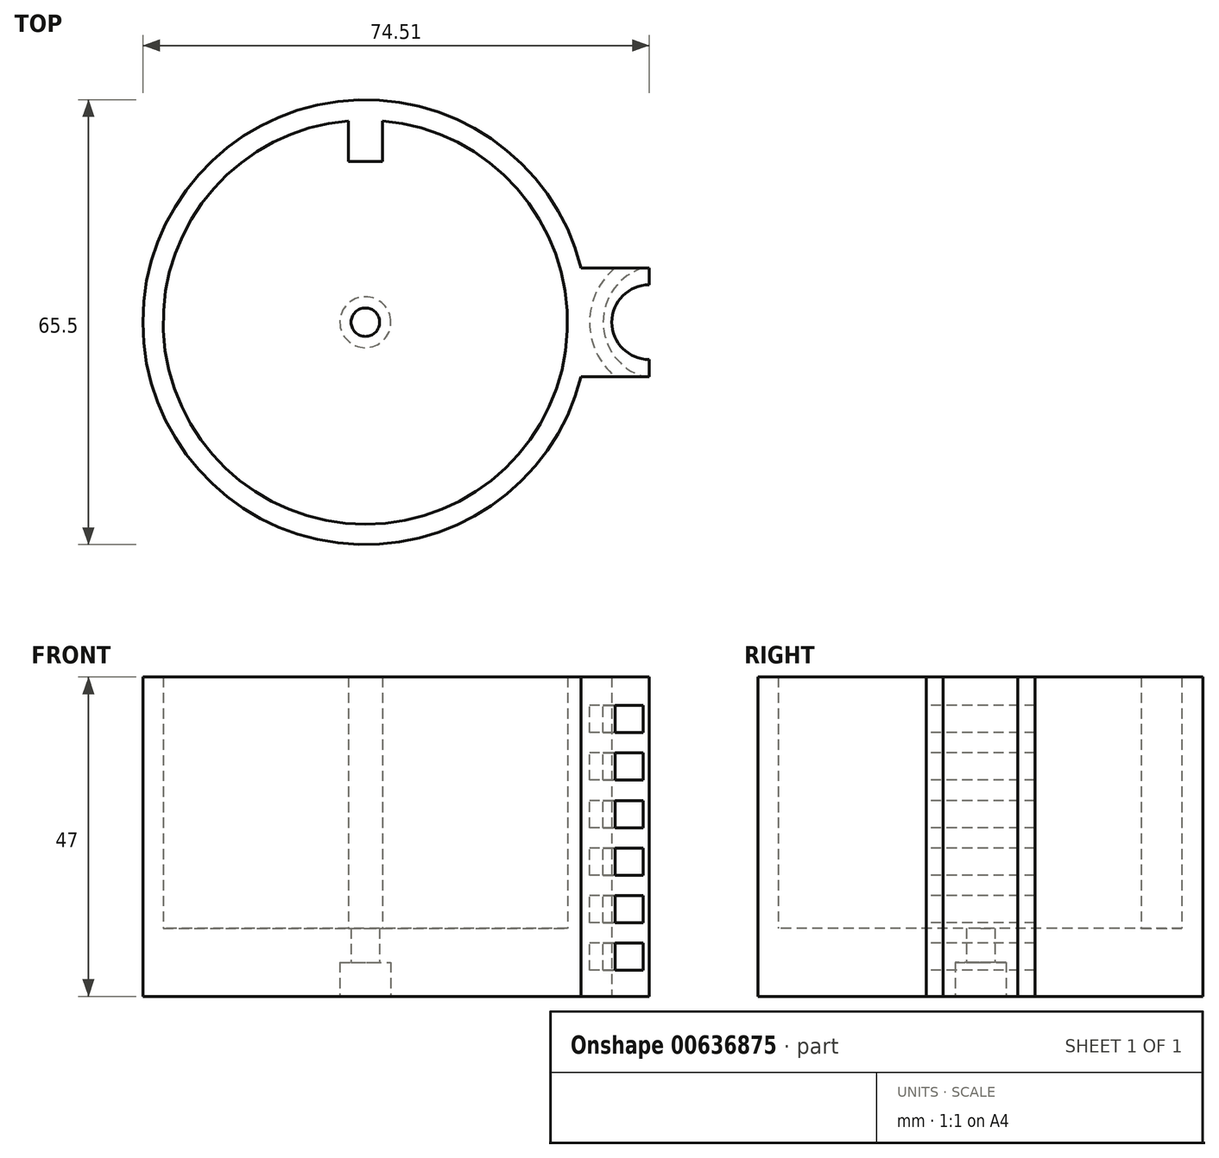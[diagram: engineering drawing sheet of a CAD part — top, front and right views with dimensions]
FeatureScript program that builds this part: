
annotation { "Feature Type Name" : "Feature", "Feature Type Description" : "" }
export const myFeature = defineFeature(function(context is Context, id is Id, definition is map)
    precondition{}
    {
        {
            var Q0;
            Q0=qCreatedBy(makeId("Top.planeOp"),FACE);
            var sketch = newSketch(context, id + "F0", { "sketchPlane" : qUnion([Q0])});
            skCircle(sketch, "E0", {"center": v(0, 0) * mm, "radius": 32.75 * mm});
            skSolve(sketch);
        }
        {
            var Q0;
            Q0=makeQuery(id+"F0.imprint","IMPRINT",FACE,{"disambiguationData":[TD([[makeQuery(id+"F0.imprint","IMPRINT",EDGE,{"derivedFrom":sQuery(id+"F0.wireOp",EDGE,"E0")}),1.0]])]});
            extrude(context, id + "F1", {"entities" : qUnion([Q0]), "depth" : 40 * mm, "offsetDistance" : 25 * mm});
        }
        {
            var Q0;
            Q0=makeQuery(id+"F1.opExtrude","CAP_FACE",FACE,{"disambiguationData":[OSD([sQuery(id+"F0.wireOp",EDGE,"E0")])],"isStart":false});
            shell(context, id + "F2", {"entities" : qUnion([Q0]), "thickness" : 3 * mm});
        }
        {
            var Q0;
            Q0=makeQuery(id+"F1.opExtrude","CAP_FACE",FACE,{"disambiguationData":[OSD([sQuery(id+"F0.wireOp",EDGE,"E0")])],"isStart":true});
            extrude(context, id + "F3", {"entities" : qUnion([Q0]), "operationType" : NewBodyOperationType.ADD, "depth" : 7 * mm, "offsetDistance" : 25 * mm});
        }
        {
            var Q0;
            Q0=makeQuery(id+"F3.opExtrude","CAP_FACE",FACE,{"disambiguationData":[OSD([sQuery(id+"F0.wireOp",EDGE,"E0")])],"isStart":false});
            var sketch = newSketch(context, id + "F4", { "sketchPlane" : qUnion([Q0])});
            skPoint(sketch, "E1", {"position": v(0, 0) * mm});
            skSolve(sketch);
        }
        {
            var Q0;
            Q0=sQuery(id+"F4.wireOp",VERTEX,"E1");
            var Q1;
            Q1=makeQuery(id+"F1.opExtrude","SWEPT_BODY",BODY,{"disambiguationData":[OSD([sQuery(id+"F0.wireOp",EDGE,"E0")])]});
            hole(context, id + "F5", {"style" : HoleStyle.C_BORE, "endStyle" : HoleEndStyle.BLIND, "holeDiameter" : 4.2 * mm, "cBoreDiameter" : 7.5 * mm, "cBoreDepth" : 5 * mm, "majorDiameter" : 4 * mm, "holeDepth" : 15 * mm, "isTappedThrough" : true, "tappedDepth" : 12 * mm, "tapClearance" : 3, "startFromSketch" : true, "locations" : qUnion([Q0]), "scope" : qUnion([Q1])});
        }
        {
            var Q0;
            {var subQ0=sQuery(id+"F0.wireOp",EDGE,"E0");Q0=makeQuery(id+"F2.opShell","OFFSET_FACE",FACE,{"disambiguationData":[OSD([subQ0]),TDD([makeQuery(id+"F1.opExtrude","CAP_FACE",FACE,{"disambiguationData":[OSD([subQ0])],"isStart":true})])]});}
            var sketch = newSketch(context, id + "F6", { "sketchPlane" : qUnion([Q0])});
            skLineSegment(sketch, "E2", {"start": v(-2.5, 29.64) * mm, "end": v(-2.5, 23.64) * mm});
            skLineSegment(sketch, "E3", {"start": v(-2.5, 23.64) * mm, "end": v(2.5, 23.64) * mm});
            skLineSegment(sketch, "E4", {"start": v(2.5, 23.64) * mm, "end": v(2.5, 29.64) * mm});
            skSolve(sketch);
        }
        {
            var Q0;
            {var subQ0=sQuery(id+"F6.wireOp",EDGE,"E2");Q0=makeQuery(id+"F6.imprint","IMPRINT",FACE,{"disambiguationData":[TD([[makeQuery(id+"F6.imprint","IMPRINT",EDGE,{"derivedFrom":subQ0}),1.0]])]});}
            extrude(context, id + "F7", {"entities" : qUnion([Q0]), "operationType" : NewBodyOperationType.ADD, "depth" : 37 * mm, "offsetDistance" : 25 * mm});
        }
        {
            var Q0;
            Q0=makeQuery(id+"F3.opExtrude","CAP_FACE",FACE,{"disambiguationData":[OSD([sQuery(id+"F0.wireOp",EDGE,"E0")])],"isStart":false});
            var sketch = newSketch(context, id + "F8", { "sketchPlane" : qUnion([Q0])});
            skLineSegment(sketch, "E5", {"start": v(31.76, -8) * mm, "end": v(41.76, -8) * mm});
            skLineSegment(sketch, "E6", {"start": v(41.76, -8) * mm, "end": v(41.76, 8) * mm});
            skLineSegment(sketch, "E7", {"start": v(41.76, 8) * mm, "end": v(31.76, 8) * mm});
            skCircle(sketch, "E8", {"center": v(41.76, 0) * mm, "radius": 5.5 * mm});
            skSolve(sketch);
        }
        {
            var Q0;
            {var subQ4=sQuery(id+"F8.wireOp",EDGE,"E5");Q0=makeQuery(id+"F8.imprint","IMPRINT",FACE,{"disambiguationData":[TD([[makeQuery(id+"F8.imprint","IMPRINT",EDGE,{"derivedFrom":subQ4}),1.0]])]});}
            extrude(context, id + "F9", {"entities" : qUnion([Q0]), "operationType" : NewBodyOperationType.ADD, "oppositeDirection" : true, "depth" : 47 * mm, "offsetDistance" : 25 * mm});
        }
        {
            var Q0;
            Q0=qCreatedBy(makeId("Front.planeOp"),FACE);
            var sketch = newSketch(context, id + "F10", { "sketchPlane" : qUnion([Q0])});
            skLineSegment(sketch, "E9.bottom", {"start": v(34.99, -3.17) * mm, "end": v(32.99, -3.17) * mm});
            skLineSegment(sketch, "E9.top", {"start": v(34.99, 0.83) * mm, "end": v(32.99, 0.83) * mm});
            skLineSegment(sketch, "E9.left", {"start": v(34.99, -3.17) * mm, "end": v(34.99, 0.83) * mm});
            skLineSegment(sketch, "E9.right", {"start": v(32.99, -3.17) * mm, "end": v(32.99, 0.83) * mm});
            skLineSegment(sketch, "E10.0.1.0", {"start": v(34.99, 3.83) * mm, "end": v(32.99, 3.83) * mm});
            skLineSegment(sketch, "E10.0.1.1", {"start": v(34.99, 7.83) * mm, "end": v(32.99, 7.83) * mm});
            skLineSegment(sketch, "E10.0.1.2", {"start": v(34.99, 3.83) * mm, "end": v(34.99, 7.83) * mm});
            skLineSegment(sketch, "E10.0.1.3", {"start": v(32.99, 3.83) * mm, "end": v(32.99, 7.83) * mm});
            skLineSegment(sketch, "E10.0.2.0", {"start": v(34.99, 10.83) * mm, "end": v(32.99, 10.83) * mm});
            skLineSegment(sketch, "E10.0.2.1", {"start": v(34.99, 14.83) * mm, "end": v(32.99, 14.83) * mm});
            skLineSegment(sketch, "E10.0.2.2", {"start": v(34.99, 10.83) * mm, "end": v(34.99, 14.83) * mm});
            skLineSegment(sketch, "E10.0.2.3", {"start": v(32.99, 10.83) * mm, "end": v(32.99, 14.83) * mm});
            skLineSegment(sketch, "E10.0.3.0", {"start": v(34.99, 17.83) * mm, "end": v(32.99, 17.83) * mm});
            skLineSegment(sketch, "E10.0.3.1", {"start": v(34.99, 21.83) * mm, "end": v(32.99, 21.83) * mm});
            skLineSegment(sketch, "E10.0.3.2", {"start": v(34.99, 17.83) * mm, "end": v(34.99, 21.83) * mm});
            skLineSegment(sketch, "E10.0.3.3", {"start": v(32.99, 17.83) * mm, "end": v(32.99, 21.83) * mm});
            skLineSegment(sketch, "E10.0.4.0", {"start": v(34.99, 24.83) * mm, "end": v(32.99, 24.83) * mm});
            skLineSegment(sketch, "E10.0.4.1", {"start": v(34.99, 28.83) * mm, "end": v(32.99, 28.83) * mm});
            skLineSegment(sketch, "E10.0.4.2", {"start": v(34.99, 24.83) * mm, "end": v(34.99, 28.83) * mm});
            skLineSegment(sketch, "E10.0.4.3", {"start": v(32.99, 24.83) * mm, "end": v(32.99, 28.83) * mm});
            skLineSegment(sketch, "E10.0.5.0", {"start": v(34.99, 31.83) * mm, "end": v(32.99, 31.83) * mm});
            skLineSegment(sketch, "E10.0.5.1", {"start": v(34.99, 35.83) * mm, "end": v(32.99, 35.83) * mm});
            skLineSegment(sketch, "E10.0.5.2", {"start": v(34.99, 31.83) * mm, "end": v(34.99, 35.83) * mm});
            skLineSegment(sketch, "E10.0.5.3", {"start": v(32.99, 31.83) * mm, "end": v(32.99, 35.83) * mm});
            skLineSegment(sketch, "E10.direction1", {"start": v(32.99, -3.17) * mm, "end": v(57.99, -3.17) * mm, "construction": true});
            skLineSegment(sketch, "E10.direction2", {"start": v(32.99, -3.17) * mm, "end": v(32.99, 3.83) * mm, "construction": true});
            skLineSegment(sketch, "E11", {"start": v(43.36, 0) * mm, "end": v(43.36, 35.77) * mm});
            skSolve(sketch);
        }
        {
            var Q0;
            Q0 = qSketchRegion(id + "F10", true);
            var Q1;
            Q1=sQuery(id+"F10.wireOp",EDGE,"E11");
            revolve(context, id + "F11", {"operationType" : NewBodyOperationType.REMOVE, "entities" : qUnion([Q0]), "axis" : qUnion([Q1]), "revolveType" : RevolveType.FULL, "oppositeDirection" : true});
        }
    });
